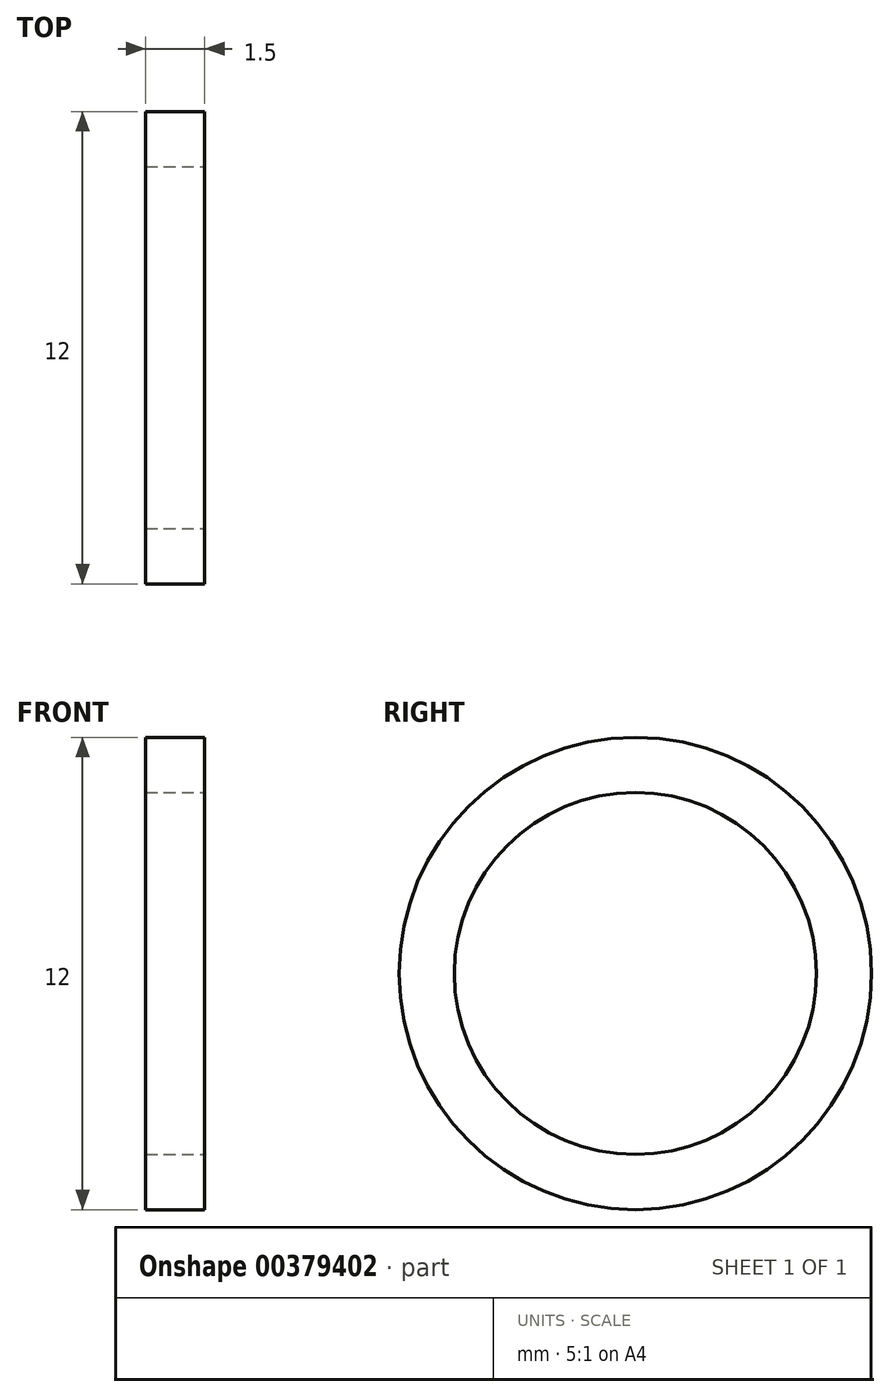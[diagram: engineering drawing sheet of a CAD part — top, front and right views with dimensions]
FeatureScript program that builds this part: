
annotation { "Feature Type Name" : "Feature", "Feature Type Description" : "" }
export const myFeature = defineFeature(function(context is Context, id is Id, definition is map)
    precondition{}
    {
        {
            var Q0;
            Q0=qCreatedBy(makeId("Front.planeOp"),FACE);
            var sketch = newSketch(context, id + "F0", { "sketchPlane" : qUnion([Q0])});
            skCircle(sketch, "E0", {"center": v(0, 0) * mm, "radius": 6 * mm});
            skSolve(sketch);
        }
        {
            var Q0;
            Q0 = qSketchRegion(id + "F0", true);
            extrude(context, id + "F1", {"entities" : qUnion([Q0]), "oppositeDirection" : true, "depth" : 1.5 * mm});
        }
        {
            var Q0;
            Q0=makeQuery(id+"F1.opExtrude","CAP_FACE",FACE,{"disambiguationData":[OSD([sQuery(id+"F0.wireOp",EDGE,"E0")])],"isStart":true});
            var sketch = newSketch(context, id + "F2", { "sketchPlane" : qUnion([Q0])});
            skCircle(sketch, "E1", {"center": v(0, 0) * mm, "radius": 4.6 * mm});
            skSolve(sketch);
        }
        {
            var Q0;
            Q0 = qSketchRegion(id + "F2", true);
            extrude(context, id + "F3", {"entities" : qUnion([Q0]), "operationType" : NewBodyOperationType.REMOVE, "endBound" : BoundingType.THROUGH_ALL, "oppositeDirection" : true, "depth" : 25 * mm});
        }
        {
            var Q0;
            Q0=makeQuery(id+"F1.opExtrude","SWEPT_BODY",BODY,{"disambiguationData":[OSD([sQuery(id+"F0.wireOp",EDGE,"E0")])]});
            var Q1;
            Q1=makeQuery(id+"F1.opExtrude","CAP_EDGE",EDGE,{"disambiguationData":[OSD([sQuery(id+"F0.wireOp",EDGE,"E0")])],"isStart":true});
            transform(context, id + "F4", {"entities" : qUnion([Q0]), "transformType" : TransformType.ROTATION, "transformAxis" : qUnion([Q1]), "angle" : 90 * degree, "makeCopy" : false});
        }
        {
            var Q0;
            Q0=qCreatedBy(makeId("Front.planeOp"),FACE);
            var sketch = newSketch(context, id + "F5", { "sketchPlane" : qUnion([Q0])});
            skLineSegment(sketch, "E2", {"start": v(0, 8.18) * mm, "end": v(0, -9.2) * mm, "construction": true});
            skLineSegment(sketch, "E3", {"start": v(0, 6.38) * mm, "end": v(0, -7.6) * mm});
            skLineSegment(sketch, "E4", {"start": v(0, -7.6) * mm, "end": v(0, 8.18) * mm});
            skSolve(sketch);
        }
        {
            var Q0;
            Q0=makeQuery(id+"F1.opExtrude","SWEPT_BODY",BODY,{"disambiguationData":[OSD([sQuery(id+"F0.wireOp",EDGE,"E0")])]});
            var Q1;
            Q1=sQuery(id+"F5.wireOp",EDGE,"E4");
            transform(context, id + "F6", {"entities" : qUnion([Q0]), "transformType" : TransformType.ROTATION, "transformAxis" : qUnion([Q1]), "angle" : 90 * degree, "makeCopy" : false});
        }
    });
